# Revit family: Grohe_SinkMixer_Essence_30504KF0
name_source: partatom
category: Plumbing Fixtures
units: mm (PartAtom-declared; Revit-internal decimal feet)

## family parameters
Cut with Voids When Loaded = No
Host = Face
OmniClass Number = 23.45.05.00
OmniClass Title = Sanitary Equipment
Part Type = Normal
Room Calculation Point = No
Round Connector Dimension = Use Diameter
Shared = No

## types (1)
- ESSENCE Sink Mixer (30504KF0)
    Assembly Code = D2010
    AssetType = Fixed
    BIMObjectName = Grohe_SinkMixer_Essence_30504KF0
    CO2NeutralProduction = GROHE is one of the first leading manufacturer within the sanitary industry having a CO2-neutral production.
    CW Connection = Yes
    ClassificationName = Uniclass2015
    ClassificationValue = Pr_40_20_87_55
    Color = Matt Black
    Cost = 0 $
    Default Elevation = 0 mm  [stored 0 ft]
    Description = ESSENCE Sink Mixer
    DimensionsDocumentLink = https://cdn.cloud.grohe.com
    DocumentationCertificates = https://www.bimstore.co
    DocumentationInstallationGuide = https://www.bimstore.co
    DocumentationLiterature = https://www.bimstore.co
    DocumentationMaintenance = https://www.bimstore.co
    DocumentationTechnical = https://www.bimstore.co
    DurationUnit = Years
    EF000003 = Top/tap hole
    EF000139 = Other
    EF001707 = 70 °C
    EF002149 = FALSE
    EF002286 = Hose (gland nut)
    EF002671 = Black
    EF007955 = FALSE
    EF011775 = not applicable
    EF011779 = FALSE
    EF011781 = not applicable
    EF012753 = 8.0
    EF014578 = FALSE
    EF014591 = FALSE
    EF016731 = Group I,<= 20 dB(A)
    EF020105 = No
    EF020780 = Single-grip
    EF020781 = Cartouche, ceramic
    EF020785 = 3/8 inch
    EF020787 = Group II, <=30 dB(A)
    EF020789 = 204 mm
    EF020791 = Brass
    EF020792 = FALSE
    EF020795 = Rotating, top
    EF020796 = 348 mm  [stored 1.14173 ft]
    EF020797 = 315 mm  [stored 1.03346 ft]
    EF020799 = TRUE
    EF020800 = FALSE
    EF020801 = FALSE
    EF020803 = FALSE
    EF020804 = FALSE
    EF020871 = FALSE
    EF020872 = TRUE
    EF020873 = FALSE
    EF021652 = FALSE
    EF021758 = TRUE
    EF021808 = 1-hole
    EF021835 = 0 mm  [stored 0 ft]
    EF022042 = Z
    EF022750 = Pipe
    EF023686 = not applicable
    EF023687 = FALSE
    EF023688 = Foam jet nozzle
    EF023957 = TRUE
    EF025109 = Other
    EF025247 = FALSE
    EFDE0022 = Group I, <=20 dB(A)
    EFSE0002 = FALSE
    Ecojoy = No
    ExpectedLife = 0
    FullRecyclabilityOfPlastic = All plastic components are fully recyclable
    GROHESocialCommittment = green.grohe.com/social_engagement
    GROHESustainability = green.grohe.com
    HW Connection = Yes
    IfcExportAs = IfcPipeFitting
    IfcExportType = IfcPipeFittingType
    Keynote = N13
    Manufacturer = Grohe
    ManufacturerName = Grohe
    Model = ESSENCE Sink Mixer
    ModelNumber = 30504KF0
    ModelReference = ESSENCE Sink Mixer
    NBSDescription = Mixer taps
    NBSObjectName = Grohe - Mixer taps
    NBSReference = 45-35-70/345
    NominalDepth = 0 mm  [stored 0 ft]
    NominalHeight = 0 mm  [stored 0 ft]
    NominalLength = 0 mm  [stored 0 ft]
    PQDiagramLink = https://cdn.cloud.grohe.com
    PrimaryMaterial = Grohe_MattBlack
    ProductDescription = high spout

single hole installation

GROHE Long-Life Shine finish

GROHE SilkMove 28 mm ceramic cartridge

GROHE EasyDock guarantees easy retraction and 

smooth docking back to the starting position

flow straightener

pull-out dual spray - switches back and forth 

between regular flow and spray

diverter: laminar spray/SpeedClean shower jet

automatic return to laminar spray

metal spray

swivel tubular spout

swivel area 360°

integrated non-return valve

protected against backflow

flexible connection hoses

metal fixation set

integrated temperature limiter

min. recommended pressure 1.0 bar

professional exclusive
    ProductNumber = 30504KF0
    ProductPageURL = https://www.grohe.co.uk
    ProductShortText = Essence Single-lever sink mixer 1/2"
    ProductType = Single Lever Mixer
    ProductionYear = 2023
    SustainabilityAward = green.grohe.com/awards
    SustainabilityReport = green.grohe.com/reporting
    Type Comments = ESSENCE Sink Mixer
    TypeName = ESSENCE Sink Mixer
    URL = https://www.grohe.co.uk
    Vent Connection = No
    WarrantyDurationLabor = 0
    WarrantyDurationParts = 0
    WarrantyDurationUnit = Years
    Waste Connection = No
    _BSBibleVersion = 17
    _BimSpecGuid = 0
    _CurrentRevision = 1
    _DistributedBy = https://www.bimstore.co
    _ObjectUserGuide = https://www.bimstore.co

note: [stored X ft] marks values corroborated as IEEE doubles in the binary element streams (Revit-internal decimal feet)

## geometry (parser evidence)
native form markers: Sweep x1
no freeform markers — native parametric forms only
